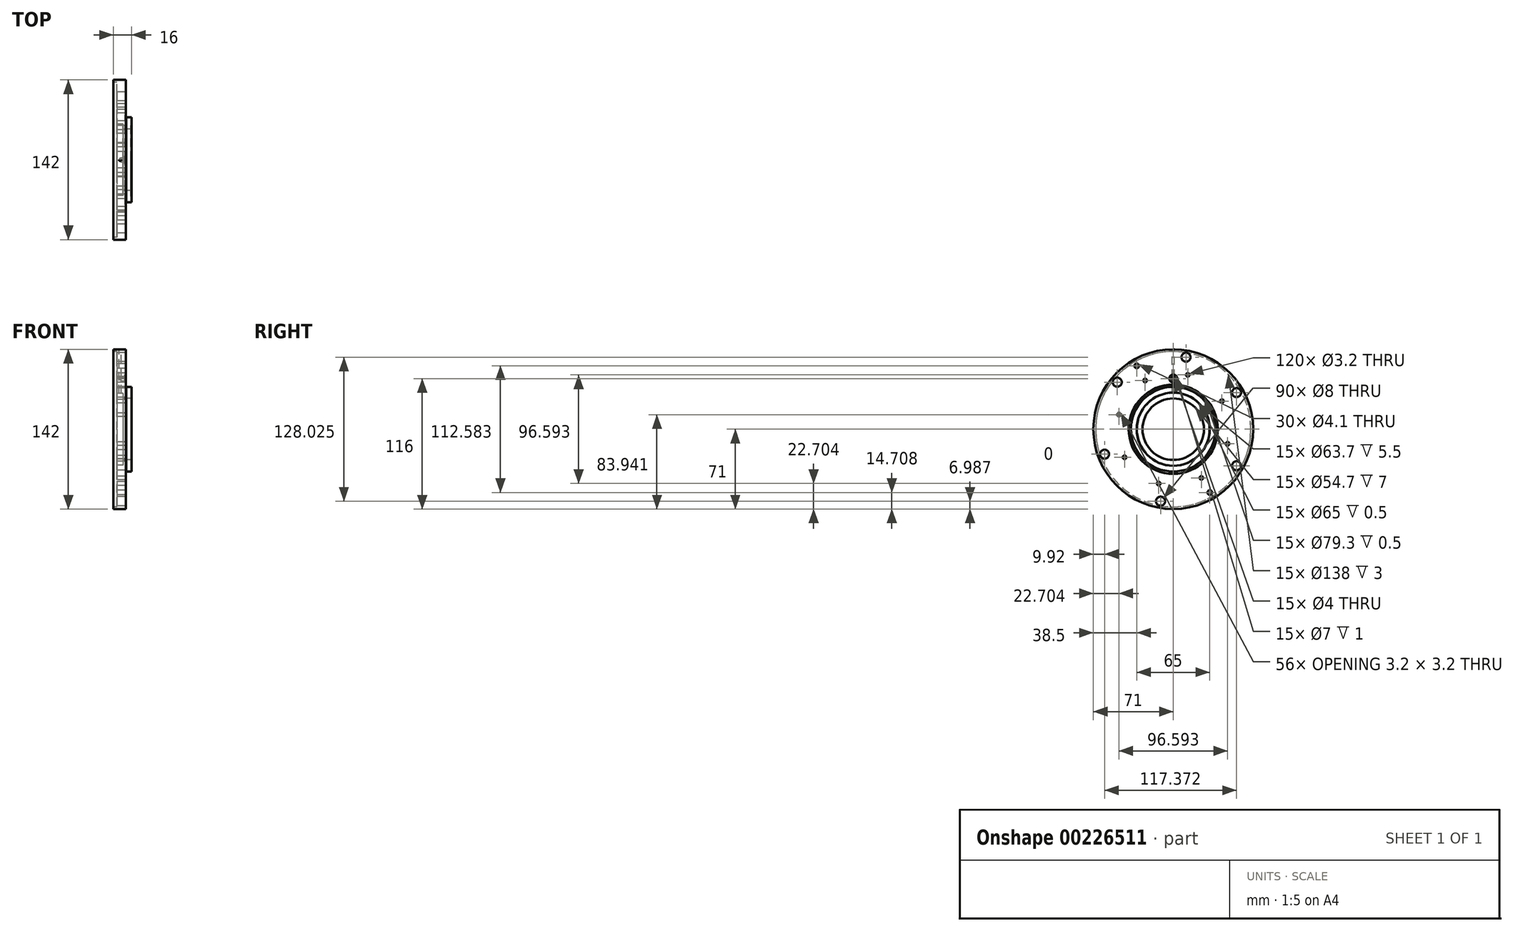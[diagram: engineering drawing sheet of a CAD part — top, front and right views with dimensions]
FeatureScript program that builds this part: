
annotation { "Feature Type Name" : "Feature", "Feature Type Description" : "" }
export const myFeature = defineFeature(function(context is Context, id is Id, definition is map)
    precondition{}
    {
        {
            var Q0;
            Q0=qCreatedBy(makeId("Front.planeOp"),FACE);
            var sketch = newSketch(context, id + "F0", { "sketchPlane" : qUnion([Q0])});
            skLineSegment(sketch, "E0", {"start": v(8, 71) * mm, "end": v(8, 39.65) * mm});
            skLineSegment(sketch, "E1", {"start": v(12.5, 32.5) * mm, "end": v(12.5, 27.35) * mm});
            skLineSegment(sketch, "E2", {"start": v(12.5, 27.35) * mm, "end": v(5.5, 27.35) * mm});
            skLineSegment(sketch, "E3", {"start": v(5.5, 27.35) * mm, "end": v(5.5, 31.85) * mm});
            skLineSegment(sketch, "E4", {"start": v(5.5, 31.85) * mm, "end": v(0, 31.85) * mm});
            skLineSegment(sketch, "E5", {"start": v(-3, 69) * mm, "end": v(-3, 71) * mm});
            skLineSegment(sketch, "E6", {"start": v(12.5, 32.5) * mm, "end": v(13, 32.5) * mm});
            skLineSegment(sketch, "E7", {"start": v(-3, 71) * mm, "end": v(8, 71) * mm});
            skLineSegment(sketch, "E8", {"start": v(-3, 69) * mm, "end": v(0, 69) * mm});
            skLineSegment(sketch, "E9", {"start": v(0, 69) * mm, "end": v(0, 31.85) * mm});
            skLineSegment(sketch, "E10", {"start": v(13, 37.65) * mm, "end": v(8.5, 37.65) * mm});
            skLineSegment(sketch, "E11", {"start": v(13, 32.5) * mm, "end": v(13, 37.65) * mm});
            skLineSegment(sketch, "E12", {"start": v(8.5, 37.65) * mm, "end": v(8.5, 37.15) * mm});
            skLineSegment(sketch, "E13", {"start": v(8.5, 37.15) * mm, "end": v(7.5, 37.15) * mm});
            skLineSegment(sketch, "E14", {"start": v(7.5, 37.15) * mm, "end": v(7.5, 39.65) * mm});
            skLineSegment(sketch, "E15", {"start": v(7.5, 39.65) * mm, "end": v(8, 39.65) * mm});
            skLineSegment(sketch, "E16", {"start": v(0, 0) * mm, "end": v(12.23, 0) * mm});
            skSolve(sketch);
        }
        {
            var Q0;
            Q0=makeQuery(id+"F0.imprint","IMPRINT",FACE,{"disambiguationData":[TD([[makeQuery(id+"F0.imprint","IMPRINT",EDGE,{"derivedFrom":sQuery(id+"F0.wireOp",EDGE,"E0")}),-1.0]])]});
            var Q1;
            Q1=sQuery(id+"F0.wireOp",EDGE,"E16");
            revolve(context, id + "F1", {"entities" : qUnion([Q0]), "axis" : qUnion([Q1]), "revolveType" : RevolveType.FULL});
        }
        {
            var Q0;
            Q0=makeQuery(id+"F1.opRevolve","SWEPT_FACE",FACE,{"disambiguationData":[OSD([sQuery(id+"F0.wireOp",EDGE,"E9")])]});
            var sketch = newSketch(context, id + "F2", { "sketchPlane" : qUnion([Q0])});
            skCircle(sketch, "E17", {"center": v(0, 0) * mm, "radius": 65 * mm});
            skLineSegment(sketch, "E18", {"start": v(0, 0) * mm, "end": v(49.8, 41.78) * mm, "construction": true});
            skLineSegment(sketch, "E19", {"start": v(0, 0) * mm, "end": v(61.08, -22.23) * mm, "construction": true});
            skLineSegment(sketch, "E20", {"start": v(0, 0) * mm, "end": v(11.29, -64.01) * mm, "construction": true});
            skLineSegment(sketch, "E21", {"start": v(0, 0) * mm, "end": v(-56.3, -32.5) * mm, "construction": true});
            skLineSegment(sketch, "E22", {"start": v(0, 0) * mm, "end": v(-56.3, 32.5) * mm, "construction": true});
            skLineSegment(sketch, "E23", {"start": v(0, 0) * mm, "end": v(-11.29, 64.01) * mm, "construction": true});
            skLineSegment(sketch, "E24", {"start": v(32.5, 56.3) * mm, "end": v(-32.5, -56.3) * mm, "construction": true});
            skPoint(sketch, "E25", {"position": v(-11.29, 64.01) * mm});
            skPoint(sketch, "E26", {"position": v(32.5, 56.3) * mm});
            skPoint(sketch, "E27", {"position": v(49.8, 41.78) * mm});
            skPoint(sketch, "E28", {"position": v(61.08, -22.23) * mm});
            skPoint(sketch, "E29", {"position": v(11.29, -64.01) * mm});
            skPoint(sketch, "E30", {"position": v(-32.5, -56.3) * mm});
            skPoint(sketch, "E31", {"position": v(-56.3, -32.5) * mm});
            skPoint(sketch, "E32", {"position": v(-56.3, 32.5) * mm});
            skCircle(sketch, "E33", {"center": v(0, 0) * mm, "radius": 50 * mm});
            skPoint(sketch, "E34", {"position": v(-43.3, 25) * mm});
            skPoint(sketch, "E35", {"position": v(-25, -43.3) * mm});
            skLineSegment(sketch, "E36", {"start": v(-12.94, 48.3) * mm, "end": v(0, 0) * mm});
            skPoint(sketch, "E37", {"position": v(-12.94, 48.3) * mm});
            skPoint(sketch, "E38", {"position": v(-48.3, -12.94) * mm});
            skPoint(sketch, "E39", {"position": v(12.94, -48.3) * mm});
            skPoint(sketch, "E40", {"position": v(43.3, -25) * mm});
            skPoint(sketch, "E41", {"position": v(48.3, 12.94) * mm});
            skPoint(sketch, "E42", {"position": v(25, 43.3) * mm});
            skLineSegment(sketch, "E43", {"start": v(0, 0) * mm, "end": v(25, 43.3) * mm});
            skLineSegment(sketch, "E44", {"start": v(0, 0) * mm, "end": v(48.3, 12.94) * mm});
            skLineSegment(sketch, "E45", {"start": v(0, 0) * mm, "end": v(43.3, -25) * mm});
            skLineSegment(sketch, "E46", {"start": v(0, 0) * mm, "end": v(12.94, -48.3) * mm});
            skLineSegment(sketch, "E47", {"start": v(0, 0) * mm, "end": v(-48.3, -12.94) * mm});
            skSolve(sketch);
        }
        {
            var Q0;
            Q0=sQuery(id+"F2.wireOp",VERTEX,"E32");
            var Q1;
            Q1=sQuery(id+"F2.wireOp",VERTEX,"E25");
            var Q2;
            Q2=sQuery(id+"F2.wireOp",VERTEX,"E27");
            var Q3;
            Q3=sQuery(id+"F2.wireOp",VERTEX,"E28");
            var Q4;
            Q4=sQuery(id+"F2.wireOp",VERTEX,"E29");
            var Q5;
            Q5=sQuery(id+"F2.wireOp",VERTEX,"E31");
            var Q6;
            Q6=makeQuery(id+"F1.opRevolve","SWEPT_BODY",BODY,{"disambiguationData":[OSD([sQuery(id+"F0.wireOp",EDGE,"E0"),sQuery(id+"F0.wireOp",EDGE,"E1"),sQuery(id+"F0.wireOp",EDGE,"E2"),sQuery(id+"F0.wireOp",EDGE,"E3"),sQuery(id+"F0.wireOp",EDGE,"E4"),sQuery(id+"F0.wireOp",EDGE,"E5"),sQuery(id+"F0.wireOp",EDGE,"E6"),sQuery(id+"F0.wireOp",EDGE,"E7"),sQuery(id+"F0.wireOp",EDGE,"E8"),sQuery(id+"F0.wireOp",EDGE,"E9"),sQuery(id+"F0.wireOp",EDGE,"E10"),sQuery(id+"F0.wireOp",EDGE,"E11"),sQuery(id+"F0.wireOp",EDGE,"E12"),sQuery(id+"F0.wireOp",EDGE,"E13"),sQuery(id+"F0.wireOp",EDGE,"E14"),sQuery(id+"F0.wireOp",EDGE,"E15")])]});
            hole(context, id + "F3", {"style" : HoleStyle.C_BORE, "endStyle" : HoleEndStyle.THROUGH, "holeDiameter" : 4.5 * mm, "cBoreDiameter" : 8 * mm, "cBoreDepth" : 8 * mm, "startFromSketch" : true, "locations" : qUnion([Q0, Q1, Q2, Q3, Q4, Q5]), "scope" : qUnion([Q6]), "isTappedThrough" : true});
        }
        {
            var Q0;
            Q0=sQuery(id+"F2.wireOp",VERTEX,"E26");
            var Q1;
            Q1=sQuery(id+"F2.wireOp",VERTEX,"E30");
            var Q2;
            Q2=makeQuery(id+"F1.opRevolve","SWEPT_BODY",BODY,{"disambiguationData":[OSD([sQuery(id+"F0.wireOp",EDGE,"E0"),sQuery(id+"F0.wireOp",EDGE,"E1"),sQuery(id+"F0.wireOp",EDGE,"E2"),sQuery(id+"F0.wireOp",EDGE,"E3"),sQuery(id+"F0.wireOp",EDGE,"E4"),sQuery(id+"F0.wireOp",EDGE,"E5"),sQuery(id+"F0.wireOp",EDGE,"E6"),sQuery(id+"F0.wireOp",EDGE,"E7"),sQuery(id+"F0.wireOp",EDGE,"E8"),sQuery(id+"F0.wireOp",EDGE,"E9"),sQuery(id+"F0.wireOp",EDGE,"E10"),sQuery(id+"F0.wireOp",EDGE,"E11"),sQuery(id+"F0.wireOp",EDGE,"E12"),sQuery(id+"F0.wireOp",EDGE,"E13"),sQuery(id+"F0.wireOp",EDGE,"E14"),sQuery(id+"F0.wireOp",EDGE,"E15")])]});
            hole(context, id + "F4", {"style" : HoleStyle.SIMPLE, "endStyle" : HoleEndStyle.THROUGH, "standardTappedOrClearance" : lookupTablePath({ "standard" : "ISO", "engagement" : "75%", "pitch" : "0.9 mm", "size" : "M5", "type" : "Tapped" }), "standardBlindInLast" : lookupTablePath({ "standard" : "ISO", "engagement" : "75%", "pitch" : "0.9 mm", "size" : "M5", "type" : "Tapped" }), "holeDiameter" : 4.1 * mm, "startFromSketch" : true, "locations" : qUnion([Q0, Q1]), "scope" : qUnion([Q2]), "isTappedThrough" : true, "showTappedDepth" : true});
        }
        {
            var Q0;
            Q0=sQuery(id+"F2.wireOp",VERTEX,"E34");
            var Q1;
            Q1=sQuery(id+"F2.wireOp",VERTEX,"E37");
            var Q2;
            Q2=sQuery(id+"F2.wireOp",VERTEX,"E42");
            var Q3;
            Q3=sQuery(id+"F2.wireOp",VERTEX,"E41");
            var Q4;
            Q4=sQuery(id+"F2.wireOp",VERTEX,"E40");
            var Q5;
            Q5=sQuery(id+"F2.wireOp",VERTEX,"E39");
            var Q6;
            Q6=sQuery(id+"F2.wireOp",VERTEX,"E35");
            var Q7;
            Q7=sQuery(id+"F2.wireOp",VERTEX,"E38");
            var Q8;
            Q8=makeQuery(id+"F1.opRevolve","SWEPT_BODY",BODY,{"disambiguationData":[OSD([sQuery(id+"F0.wireOp",EDGE,"E0"),sQuery(id+"F0.wireOp",EDGE,"E1"),sQuery(id+"F0.wireOp",EDGE,"E2"),sQuery(id+"F0.wireOp",EDGE,"E3"),sQuery(id+"F0.wireOp",EDGE,"E4"),sQuery(id+"F0.wireOp",EDGE,"E5"),sQuery(id+"F0.wireOp",EDGE,"E6"),sQuery(id+"F0.wireOp",EDGE,"E7"),sQuery(id+"F0.wireOp",EDGE,"E8"),sQuery(id+"F0.wireOp",EDGE,"E9"),sQuery(id+"F0.wireOp",EDGE,"E10"),sQuery(id+"F0.wireOp",EDGE,"E11"),sQuery(id+"F0.wireOp",EDGE,"E12"),sQuery(id+"F0.wireOp",EDGE,"E13"),sQuery(id+"F0.wireOp",EDGE,"E14"),sQuery(id+"F0.wireOp",EDGE,"E15")])]});
            hole(context, id + "F5", {"style" : HoleStyle.SIMPLE, "endStyle" : HoleEndStyle.THROUGH, "standardTappedOrClearance" : lookupTablePath({ "standard" : "ISO", "engagement" : "75%", "pitch" : "0.75 mm", "size" : "M4", "type" : "Tapped" }), "standardBlindInLast" : lookupTablePath({ "standard" : "ISO", "engagement" : "75%", "pitch" : "0.75 mm", "size" : "M4", "type" : "Tapped" }), "holeDiameter" : 3.2 * mm, "startFromSketch" : true, "locations" : qUnion([Q0, Q1, Q2, Q3, Q4, Q5, Q6, Q7]), "scope" : qUnion([Q8]), "isTappedThrough" : true, "showTappedDepth" : true});
        }
        {
            var Q0;
            Q0=qCreatedBy(makeId("Top.planeOp"),FACE);
            cPlane(context, id + "F6", {"entities" : qUnion([Q0]), "cplaneType" : CPlaneType.OFFSET, "offset" : (142 / 2) * mm, "width" : 150 * mm, "height" : 150 * mm});
        }
        {
            var Q0;
            Q0=qCreatedBy(id+"F6.planeOp",FACE);
            var sketch = newSketch(context, id + "F7", { "sketchPlane" : qUnion([Q0])});
            skPoint(sketch, "E48", {"position": v(3, 0) * mm});
            skSolve(sketch);
        }
        {
            var Q0;
            Q0=sQuery(id+"F7.wireOp",VERTEX,"E48");
            var Q1;
            Q1=makeQuery(id+"F1.opRevolve","SWEPT_BODY",BODY,{"disambiguationData":[OSD([sQuery(id+"F0.wireOp",EDGE,"E0"),sQuery(id+"F0.wireOp",EDGE,"E1"),sQuery(id+"F0.wireOp",EDGE,"E2"),sQuery(id+"F0.wireOp",EDGE,"E3"),sQuery(id+"F0.wireOp",EDGE,"E4"),sQuery(id+"F0.wireOp",EDGE,"E5"),sQuery(id+"F0.wireOp",EDGE,"E6"),sQuery(id+"F0.wireOp",EDGE,"E7"),sQuery(id+"F0.wireOp",EDGE,"E8"),sQuery(id+"F0.wireOp",EDGE,"E9"),sQuery(id+"F0.wireOp",EDGE,"E10"),sQuery(id+"F0.wireOp",EDGE,"E11"),sQuery(id+"F0.wireOp",EDGE,"E12"),sQuery(id+"F0.wireOp",EDGE,"E13"),sQuery(id+"F0.wireOp",EDGE,"E14"),sQuery(id+"F0.wireOp",EDGE,"E15")])]});
            hole(context, id + "F8", {"style" : HoleStyle.SIMPLE, "endStyle" : HoleEndStyle.BLIND, "holeDiameter" : 2 * mm, "holeDepth" : 40 * mm, "startFromSketch" : true, "locations" : qUnion([Q0]), "scope" : qUnion([Q1])});
        }
        {
            var Q0;
            Q0=makeQuery(id+"F1.opRevolve","SWEPT_FACE",FACE,{"disambiguationData":[OSD([sQuery(id+"F0.wireOp",EDGE,"E0")])]});
            var sketch = newSketch(context, id + "F9", { "sketchPlane" : qUnion([Q0])});
            skPoint(sketch, "E49", {"position": v(0, 45) * mm});
            skSolve(sketch);
        }
        {
            var Q0;
            Q0=sQuery(id+"F9.wireOp",VERTEX,"E49");
            var Q1;
            Q1=makeQuery(id+"F1.opRevolve","SWEPT_BODY",BODY,{"disambiguationData":[OSD([sQuery(id+"F0.wireOp",EDGE,"E0"),sQuery(id+"F0.wireOp",EDGE,"E1"),sQuery(id+"F0.wireOp",EDGE,"E2"),sQuery(id+"F0.wireOp",EDGE,"E3"),sQuery(id+"F0.wireOp",EDGE,"E4"),sQuery(id+"F0.wireOp",EDGE,"E5"),sQuery(id+"F0.wireOp",EDGE,"E6"),sQuery(id+"F0.wireOp",EDGE,"E7"),sQuery(id+"F0.wireOp",EDGE,"E8"),sQuery(id+"F0.wireOp",EDGE,"E9"),sQuery(id+"F0.wireOp",EDGE,"E10"),sQuery(id+"F0.wireOp",EDGE,"E11"),sQuery(id+"F0.wireOp",EDGE,"E12"),sQuery(id+"F0.wireOp",EDGE,"E13"),sQuery(id+"F0.wireOp",EDGE,"E14"),sQuery(id+"F0.wireOp",EDGE,"E15")])]});
            hole(context, id + "F10", {"style" : HoleStyle.C_BORE, "endStyle" : HoleEndStyle.BLIND, "holeDiameter" : 4 * mm, "cBoreDiameter" : 7 * mm, "cBoreDepth" : 1 * mm, "holeDepth" : 4.5 * mm, "startFromSketch" : true, "locations" : qUnion([Q0]), "scope" : qUnion([Q1])});
        }
    });
